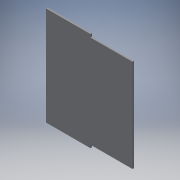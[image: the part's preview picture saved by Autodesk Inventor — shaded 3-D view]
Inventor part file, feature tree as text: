
AUTODESK INVENTOR PART (.ipt)
format: ipt  version: 2019 (Build 230136000, 136)  size: 406,016 bytes
history: native  units: mm
features: other x11, reference x9, sketch x2, extrude x2, projected_geometry x1
ambient origin geometry x8: Origin, YZ Plane, XZ Plane, XY Plane, X Axis, Y Axis, Z Axis, Center Point
bodies: Body1 (feature_tree)
feature tree (25):
  other  "Bryła1"
  sketch  "Szkic1"
  other  "Płaszczyzna konstrukcyjna1"
  extrude  "Wyciągnięcie proste3"  Depth=0.2mm
  extrude  "Wyciągnięcie proste2"  Depth=2.0mm
  reference  "Odniesienie1"
  reference  "Odniesienie2"
  reference  "Odniesienie3"
  reference  "Odniesienie4"
  reference  "Odniesienie5"
  reference  "Odniesienie6"
  reference  "Odniesienie7"
  sketch  "Szkic2"
  reference  "Odniesienie8"
  projected_geometry  "Pętla rzutowana1"
  reference  "Odniesienie9"
  parser-record x1  (decoder bookkeeping rows leaked as tree rows — omitted from the tree; the rows remain in map.json)
  other  "Zespół1.iam"
  other  "Bok2mm:1"
  other  "Przod2mm:1"
  other  "Bok2mm_MIR:1"
  other  "Tyl2:1"
  other  "mocowanie_silnika_wariant1_MIR:1"
  other  "mocowanie_silnika_wariant1:1"
  other  "MocowanieCzujnikaBazSciankiLewy:1"
note: 1 file-system path scrubbed to <path> (originals preserved in map.json)
